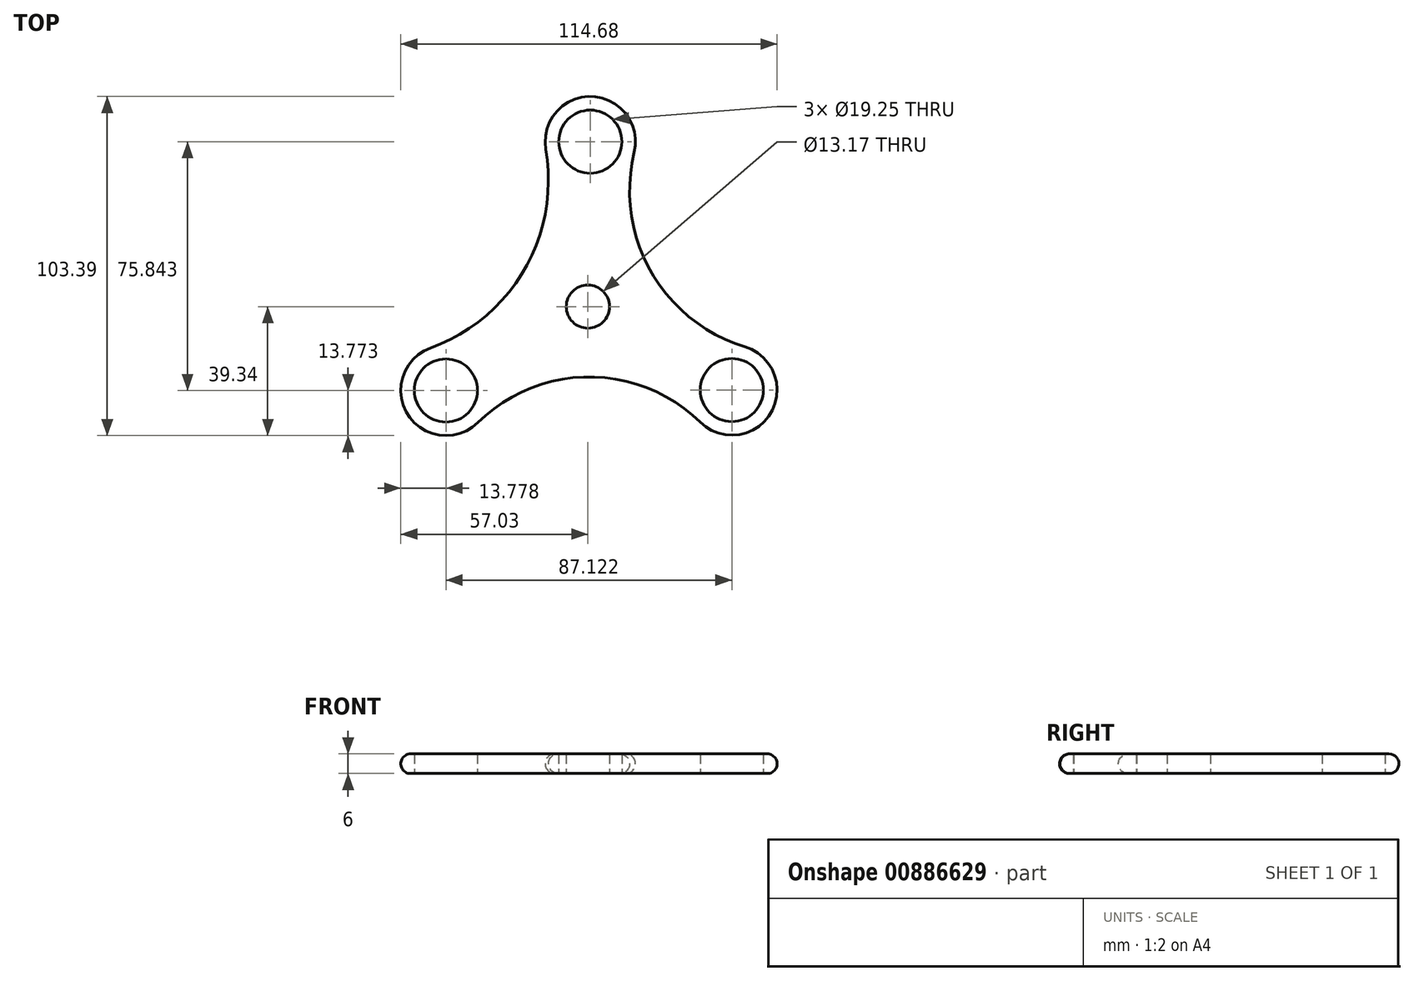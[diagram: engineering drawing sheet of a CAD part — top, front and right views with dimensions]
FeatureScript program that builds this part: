
annotation { "Feature Type Name" : "Feature", "Feature Type Description" : "" }
export const myFeature = defineFeature(function(context is Context, id is Id, definition is map)
    precondition{}
    {
        {
            var Q0;
            Q0=qCreatedBy(makeId("Top.planeOp"),FACE);
            var sketch = newSketch(context, id + "F0", { "sketchPlane" : qUnion([Q0])});
            skCircle(sketch, "E0", {"center": v(-43.25, -25.57) * mm, "radius": 9.62 * mm});
            skCircle(sketch, "E1", {"center": v(-43.25, -25.57) * mm, "radius": 13.78 * mm});
            skCircle(sketch, "E2", {"center": v(0.73, 50.28) * mm, "radius": 9.62 * mm});
            skCircle(sketch, "E3", {"center": v(0.73, 50.28) * mm, "radius": 13.78 * mm});
            skCircle(sketch, "E4", {"center": v(43.87, -25.44) * mm, "radius": 9.62 * mm});
            skCircle(sketch, "E5", {"center": v(43.87, -25.44) * mm, "radius": 13.78 * mm});
            skArc(sketch, "E6", {"start": v(14.12, 47.02) * mm, "mid": v(19.23, 10.67) * mm, "end": v(47.9, -12.26) * mm});
            skArc(sketch, "E7", {"start": v(-47.94, -12.61) * mm, "mid": v(-19.37, 11.26) * mm, "end": v(-12.84, 47.9) * mm});
            skArc(sketch, "E8", {"start": v(34.21, -35.26) * mm, "mid": v(0.3, -21.42) * mm, "end": v(-33.56, -35.36) * mm});
            skCircle(sketch, "E9", {"center": v(0, 0) * mm, "radius": 6.58 * mm});
            skCircle(sketch, "E10", {"center": v(0, 0) * mm, "radius": 9.58 * mm});
            skSolve(sketch);
        }
        {
            var Q0;
            Q0=makeQuery(id+"F0.imprint","IMPRINT",FACE,{"disambiguationData":[TD([[makeQuery(id+"F0.imprint","IMPRINT",EDGE,{"derivedFrom":sQuery(id+"F0.wireOp",EDGE,"LddEwjG8-v2lQ-nBbn-rVkt-3NlmnA4c0jJ0")}),-1.0]])]});
            var Q1;
            Q1=makeQuery(id+"F0.imprint","IMPRINT",FACE,{"disambiguationData":[TD([[makeQuery(id+"F0.imprint","IMPRINT",EDGE,{"derivedFrom":sQuery(id+"F0.wireOp",EDGE,"E0")}),-1.0]])]});
            var Q2;
            Q2=makeQuery(id+"F0.imprint","IMPRINT",FACE,{"disambiguationData":[TD([[makeQuery(id+"F0.imprint","IMPRINT",EDGE,{"derivedFrom":sQuery(id+"F0.wireOp",EDGE,"E4")}),-1.0]])]});
            var Q3;
            Q3=makeQuery(id+"F0.imprint","IMPRINT",FACE,{"disambiguationData":[TD([[makeQuery(id+"F0.imprint","IMPRINT",EDGE,{"derivedFrom":sQuery(id+"F0.wireOp",EDGE,"D0hArO8U-8Y52-Ch81-wP6f-QIYrfCcCDxRO")}),-1.0]])]});
            var Q4;
            Q4=makeQuery(id+"F0.imprint","IMPRINT",FACE,{"disambiguationData":[TD([[makeQuery(id+"F0.imprint","IMPRINT",EDGE,{"derivedFrom":sQuery(id+"F0.wireOp",EDGE,"E2")}),-1.0]])]});
            var Q5;
            {var subQ0=sQuery(id+"F0.wireOp",EDGE,"E6");Q5=makeQuery(id+"F0.imprint","IMPRINT",FACE,{"disambiguationData":[TD([[makeQuery(id+"F0.imprint","IMPRINT",EDGE,{"derivedFrom":subQ0}),-1.0]])]});}
            var Q6;
            Q6=makeQuery(id+"F0.imprint","IMPRINT",FACE,{"disambiguationData":[TD([[makeQuery(id+"F0.imprint","IMPRINT",EDGE,{"derivedFrom":sQuery(id+"F0.wireOp",EDGE,"E9")}),-1.0]])]});
            extrude(context, id + "F1", {"entities" : qUnion([Q0, Q1, Q2, Q3, Q4, Q5, Q6]), "depth" : 6 * mm, "offsetDistance" : 25 * mm});
        }
        {
            var Q0;
            Q0=makeQuery(id+"F1.opExtrude","CAP_EDGE",EDGE,{"disambiguationData":[OSD([sQuery(id+"F0.wireOp",EDGE,"E6")])],"isStart":false});
            var Q1;
            Q1=makeQuery(id+"F1.opExtrude","CAP_EDGE",EDGE,{"disambiguationData":[OSD([sQuery(id+"F0.wireOp",EDGE,"E6")])],"isStart":true});
            fillet(context, id + "F2", {"entities" : qUnion([Q0, Q1]), "radius" : 3 * mm, "tangentPropagation" : true, "allowEdgeOverflow" : false});
        }
    });
